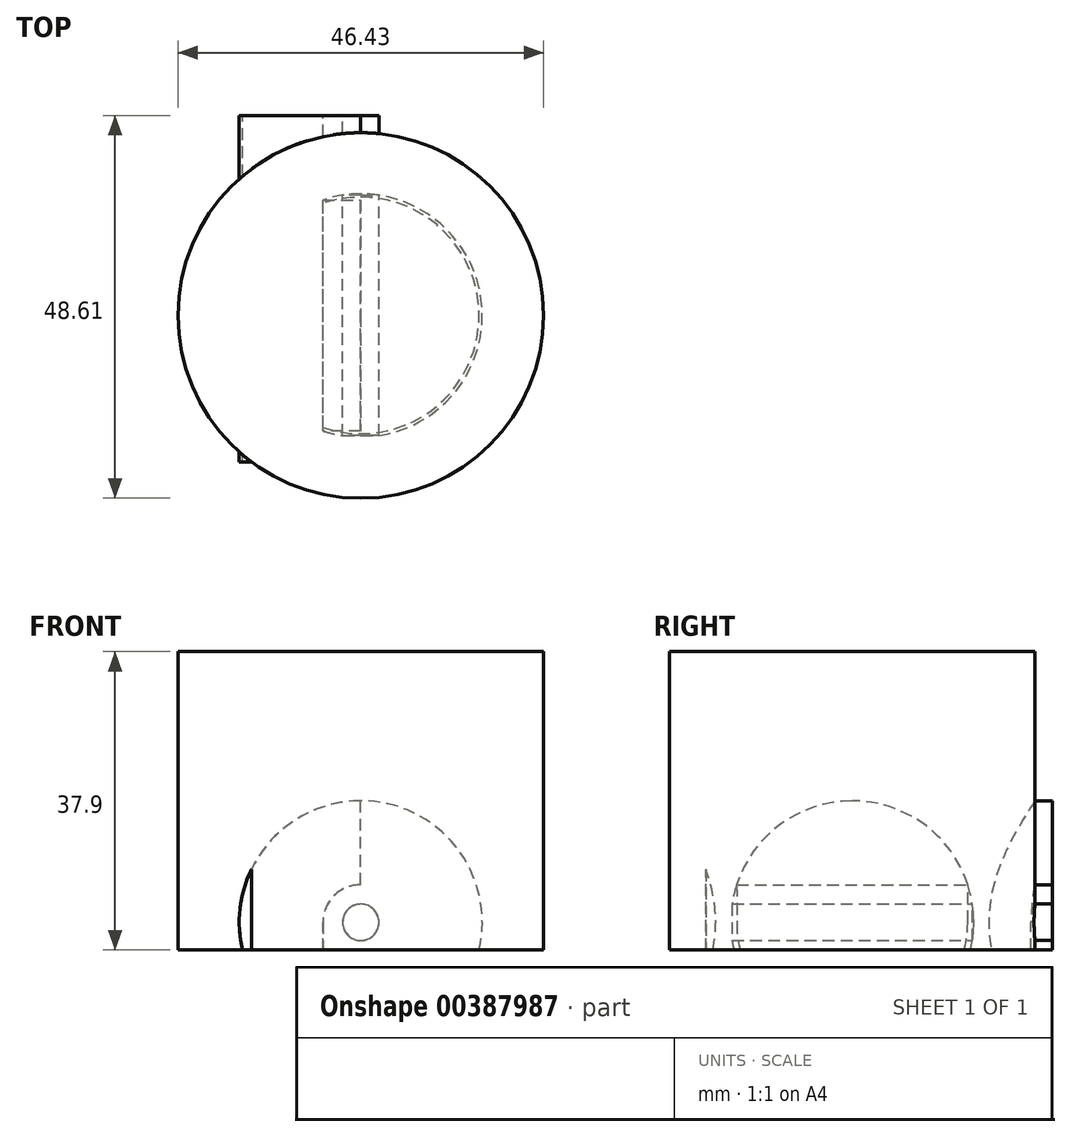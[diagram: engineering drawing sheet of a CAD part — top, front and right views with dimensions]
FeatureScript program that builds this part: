
annotation { "Feature Type Name" : "Feature", "Feature Type Description" : "" }
export const myFeature = defineFeature(function(context is Context, id is Id, definition is map)
    precondition{}
    {
        {
            var Q0;
            Q0=qCreatedBy(makeId("Front.planeOp"),FACE);
            var sketch = newSketch(context, id + "F0", { "sketchPlane" : qUnion([Q0])});
            skLineSegment(sketch, "E0.bottom", {"start": v(23.28, 18.95) * mm, "end": v(-23.28, 18.95) * mm});
            skLineSegment(sketch, "E0.top", {"start": v(23.28, -18.95) * mm, "end": v(-23.28, -18.95) * mm});
            skLineSegment(sketch, "E0.left", {"start": v(23.28, 18.95) * mm, "end": v(23.28, -18.95) * mm});
            skLineSegment(sketch, "E0.right", {"start": v(-23.28, 18.95) * mm, "end": v(-23.28, -18.95) * mm});
            skPoint(sketch, "E0.middle", {"position": v(0, 0) * mm});
            skArc(sketch, "E1", {"start": v(15.1, -18.95) * mm, "mid": v(0.06, 0) * mm, "end": v(-14.97, -18.95) * mm});
            skLineSegment(sketch, "E2.bottom", {"start": v(-4.74, -15.42) * mm, "end": v(4.74, -15.42) * mm});
            skLineSegment(sketch, "E2.top", {"start": v(-4.74, -64.5) * mm, "end": v(4.74, -64.5) * mm});
            skLineSegment(sketch, "E2.left", {"start": v(-4.74, -15.42) * mm, "end": v(-4.74, -64.5) * mm});
            skLineSegment(sketch, "E2.right", {"start": v(4.74, -15.42) * mm, "end": v(4.74, -64.5) * mm});
            skPoint(sketch, "E2.middle", {"position": v(0, -39.96) * mm});
            skArc(sketch, "E3", {"start": v(4.74, -15.42) * mm, "mid": v(0, -10.67) * mm, "end": v(-4.74, -15.42) * mm});
            skArc(sketch, "E4", {"start": v(-4.74, -64.5) * mm, "mid": v(0, -69.24) * mm, "end": v(4.74, -64.5) * mm});
            skLineSegment(sketch, "E5", {"start": v(0.06, 18.95) * mm, "end": v(0.06, -18.95) * mm});
            skLineSegment(sketch, "E6", {"start": v(0.06, -18.95) * mm, "end": v(0, -64.5) * mm});
            skLineSegment(sketch, "E7", {"start": v(0, -64.5) * mm, "end": v(0, -69.24) * mm});
            skCircle(sketch, "E8", {"center": v(0.06, -15.44) * mm, "radius": 2.31 * mm});
            skSolve(sketch);
        }
        {
            var Q0;
            {var subQ0=sQuery(id+"F0.wireOp",EDGE,"E0.left");Q0=makeQuery(id+"F0.imprint","IMPRINT",FACE,{"disambiguationData":[TD([[makeQuery(id+"F0.imprint","IMPRINT",EDGE,{"derivedFrom":subQ0}),-1.0]])]});}
            var Q1;
            Q1=sQuery(id+"F0.wireOp",EDGE,"E5");
            revolve(context, id + "F1", {"entities" : qUnion([Q0]), "axis" : qUnion([Q1]), "revolveType" : RevolveType.FULL});
        }
        {
            var Q0;
            {var subQ0=sQuery(id+"F0.wireOp",EDGE,"E5");var subQ1=sQuery(id+"F0.wireOp",EDGE,"E2.bottom");var subQ2=makeQuery(id+"F0.imprint","INTERSECT",VERTEX,{"derivedFrom":[subQ1,subQ0]});Q0=makeQuery(id+"F0.imprint","IMPRINT",FACE,{"disambiguationData":[TD([[makeQuery(id+"F0.imprint","IMPRINT",EDGE,{"disambiguationData":[TD([[subQ2,-1.0]])],"derivedFrom":subQ1}),1.0]])]});}
            var Q1;
            {var subQ0=sQuery(id+"F0.wireOp",EDGE,"E5");var subQ1=sQuery(id+"F0.wireOp",EDGE,"E2.bottom");var subQ2=makeQuery(id+"F0.imprint","INTERSECT",VERTEX,{"derivedFrom":[subQ1,subQ0]});Q1=makeQuery(id+"F0.imprint","IMPRINT",FACE,{"disambiguationData":[TD([[makeQuery(id+"F0.imprint","IMPRINT",EDGE,{"disambiguationData":[TD([[subQ2,-1.0]])],"derivedFrom":subQ1}),-1.0]])]});}
            var Q2;
            {var subQ0=sQuery(id+"F0.wireOp",EDGE,"E8");var subQ1=sQuery(id+"F0.wireOp",EDGE,"E2.bottom");var subQ2=makeQuery(id+"F0.imprint","INTERSECT",VERTEX,{"disambiguationData":[OD(0.0)],"derivedFrom":[subQ1,subQ0]});Q2=makeQuery(id+"F0.imprint","IMPRINT",FACE,{"disambiguationData":[TD([[makeQuery(id+"F0.imprint","IMPRINT",EDGE,{"disambiguationData":[TD([[subQ2,-1.0]])],"derivedFrom":subQ1}),-1.0]])]});}
            var Q3;
            {var subQ0=sQuery(id+"F0.wireOp",EDGE,"E8");var subQ1=sQuery(id+"F0.wireOp",EDGE,"E2.bottom");var subQ2=makeQuery(id+"F0.imprint","INTERSECT",VERTEX,{"disambiguationData":[OD(0.0)],"derivedFrom":[subQ1,subQ0]});Q3=makeQuery(id+"F0.imprint","IMPRINT",FACE,{"disambiguationData":[TD([[makeQuery(id+"F0.imprint","IMPRINT",EDGE,{"disambiguationData":[TD([[subQ2,-1.0]])],"derivedFrom":subQ1}),1.0]])]});}
            var Q4;
            {var subQ5=sQuery(id+"F0.wireOp",EDGE,"E0.top");var subQ7=sQuery(id+"F0.wireOp",EDGE,"E1");var subQ8=makeQuery(id+"F0.imprint","INTERSECT",VERTEX,{"disambiguationData":[OD(1.0)],"derivedFrom":[subQ5,subQ7]});Q4=makeQuery(id+"F0.imprint","IMPRINT",FACE,{"disambiguationData":[TD([[makeQuery(id+"F0.imprint","IMPRINT",EDGE,{"disambiguationData":[TD([[subQ8,1.0]])],"derivedFrom":subQ5}),-1.0]])]});}
            extrude(context, id + "F2", {"entities" : qUnion([Q0, Q1, Q2, Q3, Q4]), "operationType" : NewBodyOperationType.ADD, "depth" : 18.6 * mm, "hasSecondDirection" : true, "secondDirectionOppositeDirection" : true, "secondDirectionDepth" : 25.4 * mm});
        }
    });
